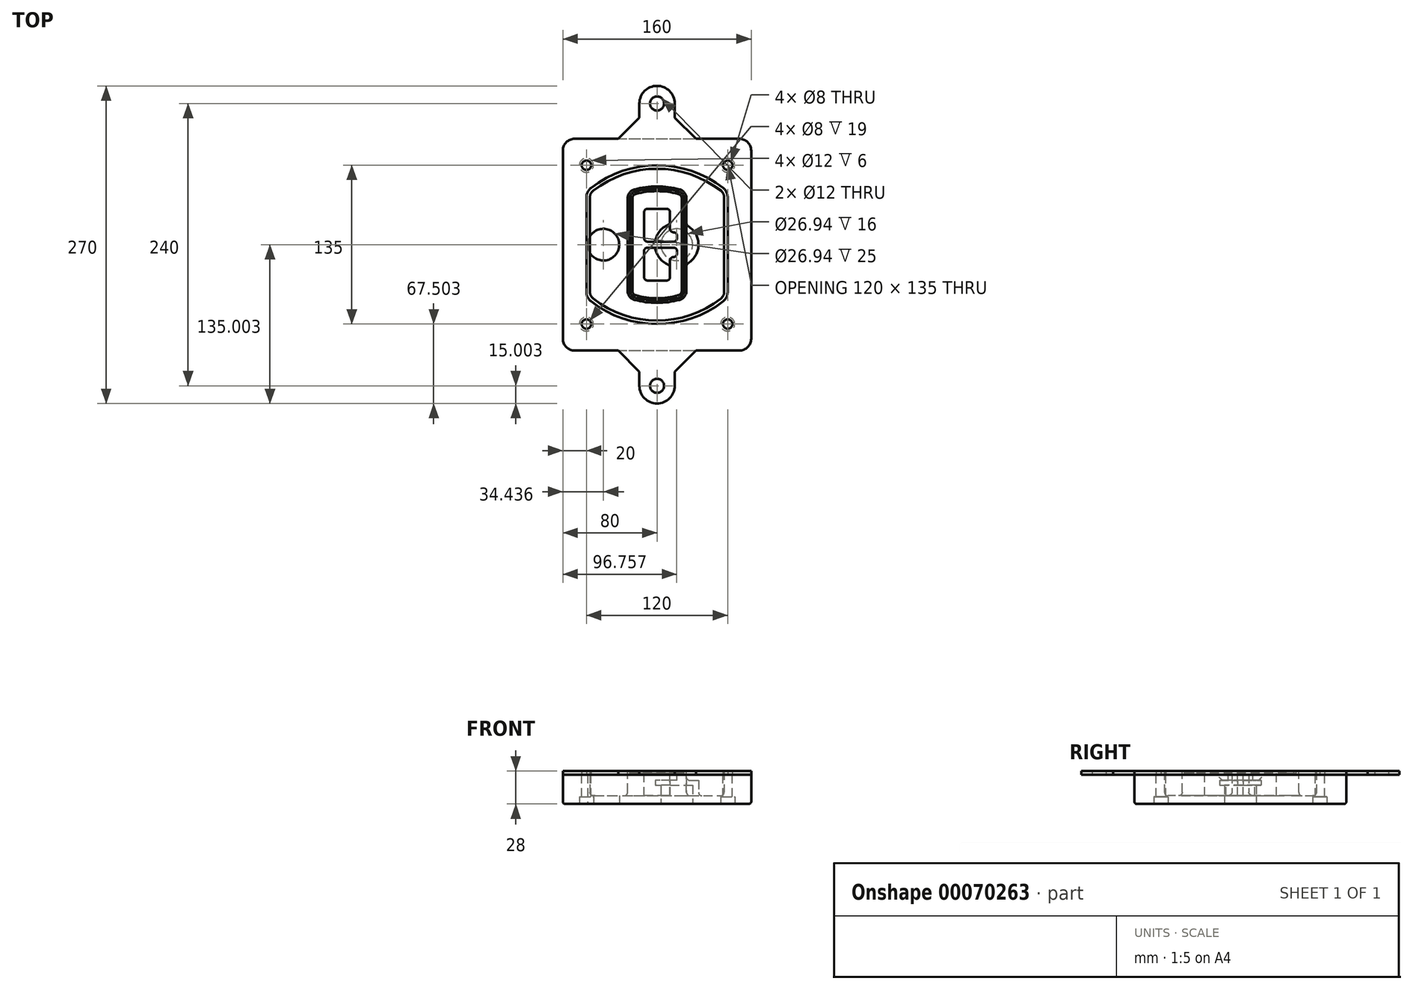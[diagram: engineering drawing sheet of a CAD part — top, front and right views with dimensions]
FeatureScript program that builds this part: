
annotation { "Feature Type Name" : "Feature", "Feature Type Description" : "" }
export const myFeature = defineFeature(function(context is Context, id is Id, definition is map)
    precondition{}
    {
        {
            var Q0;
            Q0=qCreatedBy(makeId("Top.planeOp"),FACE);
            var sketch = newSketch(context, id + "F0", { "sketchPlane" : qUnion([Q0])});
            skPoint(sketch, "E0.rect.middle", {"position": v(0, 0) * mm});
            skLineSegment(sketch, "E1.bottom", {"start": v(24.05, 28.38) * mm, "end": v(164.05, 28.38) * mm});
            skLineSegment(sketch, "E1.top", {"start": v(24.05, 208.38) * mm, "end": v(164.05, 208.38) * mm});
            skLineSegment(sketch, "E1.left", {"start": v(14.05, 38.38) * mm, "end": v(14.05, 198.38) * mm});
            skLineSegment(sketch, "E1.right", {"start": v(174.05, 38.38) * mm, "end": v(174.05, 198.38) * mm});
            skLineSegment(sketch, "E2", {"start": v(14.05, 208.38) * mm, "end": v(174.05, 28.38) * mm, "construction": true});
            skLineSegment(sketch, "E3", {"start": v(174.05, 208.38) * mm, "end": v(14.05, 28.38) * mm, "construction": true});
            skCircle(sketch, "E4", {"center": v(34.05, 185.88) * mm, "radius": 4 * mm});
            skCircle(sketch, "E5", {"center": v(154.05, 185.88) * mm, "radius": 4 * mm});
            skCircle(sketch, "E6", {"center": v(154.05, 50.88) * mm, "radius": 4 * mm});
            skCircle(sketch, "E7", {"center": v(34.05, 50.88) * mm, "radius": 4 * mm});
            skLineSegment(sketch, "E8", {"start": v(34.05, 185.88) * mm, "end": v(154.05, 185.88) * mm, "construction": true});
            skLineSegment(sketch, "E9", {"start": v(154.05, 185.88) * mm, "end": v(154.05, 50.88) * mm, "construction": true});
            skLineSegment(sketch, "E10", {"start": v(154.05, 50.88) * mm, "end": v(34.05, 50.88) * mm, "construction": true});
            skLineSegment(sketch, "E11", {"start": v(34.05, 50.88) * mm, "end": v(34.05, 185.88) * mm, "construction": true});
            skLineSegment(sketch, "E12", {"start": v(34.05, 158.68) * mm, "end": v(34.05, 78.09) * mm});
            skLineSegment(sketch, "E13", {"start": v(154.05, 158.68) * mm, "end": v(154.05, 78.09) * mm});
            skArc(sketch, "E14", {"start": v(150.2, 166.56) * mm, "mid": v(94.05, 185.88) * mm, "end": v(37.9, 166.56) * mm});
            skArc(sketch, "E15", {"start": v(37.9, 70.2) * mm, "mid": v(94.05, 50.88) * mm, "end": v(150.2, 70.2) * mm});
            skLineSegment(sketch, "E16", {"start": v(34.05, 118.38) * mm, "end": v(154.05, 118.38) * mm, "construction": true});
            skPoint(sketch, "E17.visualSharp", {"position": v(34.05, 73.38) * mm});
            skArc(sketch, "E17.filletArc", {"start": v(34.05, 78.09) * mm, "mid": v(35.06, 73.7) * mm, "end": v(37.9, 70.2) * mm});
            skPoint(sketch, "E18.visualSharp", {"position": v(34.05, 163.38) * mm});
            skArc(sketch, "E18.filletArc", {"start": v(37.9, 166.56) * mm, "mid": v(35.06, 163.06) * mm, "end": v(34.05, 158.68) * mm});
            skPoint(sketch, "E19.visualSharp", {"position": v(154.05, 163.38) * mm});
            skArc(sketch, "E19.filletArc", {"start": v(154.05, 158.68) * mm, "mid": v(153.04, 163.06) * mm, "end": v(150.2, 166.56) * mm});
            skPoint(sketch, "E20.visualSharp", {"position": v(154.05, 73.38) * mm});
            skArc(sketch, "E20.filletArc", {"start": v(150.2, 70.2) * mm, "mid": v(153.04, 73.7) * mm, "end": v(154.05, 78.09) * mm});
            skPoint(sketch, "E21.visualSharp", {"position": v(14.05, 208.38) * mm});
            skArc(sketch, "E21.filletArc", {"start": v(24.05, 208.38) * mm, "mid": v(16.98, 205.45) * mm, "end": v(14.05, 198.38) * mm});
            skPoint(sketch, "E22.visualSharp", {"position": v(174.05, 208.38) * mm});
            skArc(sketch, "E22.filletArc", {"start": v(174.05, 198.38) * mm, "mid": v(171.12, 205.45) * mm, "end": v(164.05, 208.38) * mm});
            skPoint(sketch, "E23.visualSharp", {"position": v(174.05, 28.38) * mm});
            skArc(sketch, "E23.filletArc", {"start": v(164.05, 28.38) * mm, "mid": v(171.12, 31.31) * mm, "end": v(174.05, 38.38) * mm});
            skPoint(sketch, "E24.visualSharp", {"position": v(14.05, 28.38) * mm});
            skArc(sketch, "E24.filletArc", {"start": v(14.05, 38.38) * mm, "mid": v(16.98, 31.31) * mm, "end": v(24.05, 28.38) * mm});
            skArc(sketch, "E25.0", {"start": v(151.05, 158.68) * mm, "mid": v(150.34, 161.75) * mm, "end": v(148.36, 164.2) * mm});
            skLineSegment(sketch, "E25.1", {"start": v(151.05, 158.68) * mm, "end": v(151.05, 78.09) * mm});
            skArc(sketch, "E25.2", {"start": v(148.36, 72.57) * mm, "mid": v(150.34, 75.02) * mm, "end": v(151.05, 78.09) * mm});
            skArc(sketch, "E25.3", {"start": v(39.74, 72.57) * mm, "mid": v(94.05, 53.88) * mm, "end": v(148.36, 72.57) * mm});
            skArc(sketch, "E25.4", {"start": v(37.05, 78.09) * mm, "mid": v(37.76, 75.02) * mm, "end": v(39.74, 72.57) * mm});
            skArc(sketch, "E25.5", {"start": v(148.36, 164.2) * mm, "mid": v(94.05, 182.88) * mm, "end": v(39.74, 164.2) * mm});
            skLineSegment(sketch, "E25.6", {"start": v(37.05, 158.68) * mm, "end": v(37.05, 78.09) * mm});
            skArc(sketch, "E25.7", {"start": v(39.74, 164.2) * mm, "mid": v(37.76, 161.75) * mm, "end": v(37.05, 158.68) * mm});
            skArc(sketch, "E26.0", {"start": v(35.43, 169.71) * mm, "mid": v(31.47, 164.82) * mm, "end": v(30.05, 158.68) * mm});
            skArc(sketch, "E26.1", {"start": v(152.67, 169.71) * mm, "mid": v(94.05, 189.88) * mm, "end": v(35.43, 169.71) * mm});
            skArc(sketch, "E26.2", {"start": v(158.05, 158.68) * mm, "mid": v(156.63, 164.82) * mm, "end": v(152.67, 169.71) * mm});
            skLineSegment(sketch, "E26.3", {"start": v(158.05, 158.68) * mm, "end": v(158.05, 78.09) * mm});
            skArc(sketch, "E26.4", {"start": v(152.67, 67.05) * mm, "mid": v(156.63, 71.95) * mm, "end": v(158.05, 78.09) * mm});
            skLineSegment(sketch, "E26.5", {"start": v(30.05, 158.68) * mm, "end": v(30.05, 78.09) * mm});
            skArc(sketch, "E26.6", {"start": v(35.43, 67.05) * mm, "mid": v(94.05, 46.88) * mm, "end": v(152.67, 67.05) * mm});
            skArc(sketch, "E26.7", {"start": v(30.05, 78.09) * mm, "mid": v(31.47, 71.95) * mm, "end": v(35.43, 67.05) * mm});
            skSolve(sketch);
        }
        {
            var Q0;
            Q0=makeQuery(id+"F0.imprint","IMPRINT",FACE,{"disambiguationData":[TD([[makeQuery(id+"F0.imprint","IMPRINT",EDGE,{"derivedFrom":sQuery(id+"F0.wireOp",EDGE,"E1.bottom")}),1.0]])]});
            var Q1;
            Q1=makeQuery(id+"F0.imprint","IMPRINT",FACE,{"disambiguationData":[TD([[makeQuery(id+"F0.imprint","IMPRINT",EDGE,{"derivedFrom":sQuery(id+"F0.wireOp",EDGE,"E12")}),1.0]])]});
            var Q2;
            Q2=makeQuery(id+"F0.imprint","IMPRINT",FACE,{"disambiguationData":[TD([[makeQuery(id+"F0.imprint","IMPRINT",EDGE,{"derivedFrom":sQuery(id+"F0.wireOp",EDGE,"E25.0")}),1.0]])]});
            var Q3;
            Q3=makeQuery(id+"F0.imprint","IMPRINT",FACE,{"disambiguationData":[TD([[makeQuery(id+"F0.imprint","IMPRINT",EDGE,{"derivedFrom":sQuery(id+"F0.wireOp",EDGE,"E12")}),-1.0]])]});
            extrude(context, id + "F1", {"entities" : qUnion([Q0, Q1, Q2, Q3]), "oppositeDirection" : true, "depth" : 25 * mm});
        }
        {
            var Q0;
            Q0=makeQuery(id+"F0.imprint","IMPRINT",FACE,{"disambiguationData":[TD([[makeQuery(id+"F0.imprint","IMPRINT",EDGE,{"derivedFrom":sQuery(id+"F0.wireOp",EDGE,"E12")}),1.0]])]});
            extrude(context, id + "F2", {"entities" : qUnion([Q0]), "operationType" : NewBodyOperationType.ADD, "depth" : 3 * mm});
        }
        {
            var Q0;
            Q0=makeQuery(id+"F0.imprint","IMPRINT",FACE,{"disambiguationData":[TD([[makeQuery(id+"F0.imprint","IMPRINT",EDGE,{"derivedFrom":sQuery(id+"F0.wireOp",EDGE,"E25.0")}),1.0]])]});
            extrude(context, id + "F3", {"entities" : qUnion([Q0]), "operationType" : NewBodyOperationType.REMOVE, "oppositeDirection" : true, "depth" : 18 * mm});
        }
        {
            var Q0;
            Q0=makeQuery(id+"F2.opExtrude","CAP_FACE",FACE,{"disambiguationData":[OSD([sQuery(id+"F0.wireOp",EDGE,"E12"),sQuery(id+"F0.wireOp",EDGE,"E13"),sQuery(id+"F0.wireOp",EDGE,"E14"),sQuery(id+"F0.wireOp",EDGE,"E15"),sQuery(id+"F0.wireOp",EDGE,"E17.filletArc"),sQuery(id+"F0.wireOp",EDGE,"E18.filletArc"),sQuery(id+"F0.wireOp",EDGE,"E19.filletArc"),sQuery(id+"F0.wireOp",EDGE,"E20.filletArc"),sQuery(id+"F0.wireOp",EDGE,"E25.0"),sQuery(id+"F0.wireOp",EDGE,"E25.1"),sQuery(id+"F0.wireOp",EDGE,"E25.2"),sQuery(id+"F0.wireOp",EDGE,"E25.3"),sQuery(id+"F0.wireOp",EDGE,"E25.4"),sQuery(id+"F0.wireOp",EDGE,"E25.5"),sQuery(id+"F0.wireOp",EDGE,"E25.6"),sQuery(id+"F0.wireOp",EDGE,"E25.7")])],"isStart":false});
            var sketch = newSketch(context, id + "F4", { "sketchPlane" : qUnion([Q0])});
            skArc(sketch, "E27.0", {"start": v(74.97, 71.41) * mm, "mid": v(94.05, 68.88) * mm, "end": v(113.13, 71.41) * mm});
            skArc(sketch, "E28.0", {"start": v(113.13, 165.35) * mm, "mid": v(94.05, 167.88) * mm, "end": v(74.97, 165.35) * mm});
            skLineSegment(sketch, "E29", {"start": v(69.05, 157.63) * mm, "end": v(69.05, 79.14) * mm});
            skLineSegment(sketch, "E30", {"start": v(119.05, 157.63) * mm, "end": v(119.05, 79.14) * mm});
            skLineSegment(sketch, "E31", {"start": v(69.05, 163.48) * mm, "end": v(119.05, 163.48) * mm, "construction": true});
            skLineSegment(sketch, "E32", {"start": v(69.05, 73.28) * mm, "end": v(119.05, 73.28) * mm, "construction": true});
            skPoint(sketch, "E33.visualSharp", {"position": v(69.05, 163.48) * mm});
            skArc(sketch, "E33.filletArc", {"start": v(74.97, 165.35) * mm, "mid": v(70.7, 162.5) * mm, "end": v(69.05, 157.63) * mm});
            skPoint(sketch, "E34.visualSharp", {"position": v(119.05, 163.48) * mm});
            skArc(sketch, "E34.filletArc", {"start": v(119.05, 157.63) * mm, "mid": v(117.4, 162.5) * mm, "end": v(113.13, 165.35) * mm});
            skPoint(sketch, "E35.visualSharp", {"position": v(119.05, 73.28) * mm});
            skArc(sketch, "E35.filletArc", {"start": v(113.13, 71.41) * mm, "mid": v(117.4, 74.27) * mm, "end": v(119.05, 79.14) * mm});
            skPoint(sketch, "E36.visualSharp", {"position": v(69.05, 73.28) * mm});
            skArc(sketch, "E36.filletArc", {"start": v(69.05, 79.14) * mm, "mid": v(70.7, 74.27) * mm, "end": v(74.97, 71.41) * mm});
            skArc(sketch, "E37.0", {"start": v(148.36, 164.2) * mm, "mid": v(94.05, 182.88) * mm, "end": v(39.74, 164.2) * mm});
            skArc(sketch, "E37.1", {"start": v(39.74, 164.2) * mm, "mid": v(37.76, 161.75) * mm, "end": v(37.05, 158.68) * mm});
            skLineSegment(sketch, "E37.2", {"start": v(37.05, 158.68) * mm, "end": v(37.05, 78.09) * mm});
            skArc(sketch, "E37.3", {"start": v(37.05, 78.09) * mm, "mid": v(37.76, 75.02) * mm, "end": v(39.74, 72.57) * mm});
            skArc(sketch, "E37.4", {"start": v(39.74, 72.57) * mm, "mid": v(94.05, 53.88) * mm, "end": v(148.36, 72.57) * mm});
            skArc(sketch, "E37.5", {"start": v(148.36, 72.57) * mm, "mid": v(150.34, 75.02) * mm, "end": v(151.05, 78.09) * mm});
            skLineSegment(sketch, "E37.6", {"start": v(151.05, 158.68) * mm, "end": v(151.05, 78.09) * mm});
            skArc(sketch, "E37.7", {"start": v(151.05, 158.68) * mm, "mid": v(150.34, 161.75) * mm, "end": v(148.36, 164.2) * mm});
            skLineSegment(sketch, "E38.0", {"start": v(117.05, 157.63) * mm, "end": v(117.05, 79.14) * mm});
            skArc(sketch, "E38.1", {"start": v(112.61, 73.34) * mm, "mid": v(115.81, 75.49) * mm, "end": v(117.05, 79.14) * mm});
            skArc(sketch, "E38.2", {"start": v(75.49, 73.34) * mm, "mid": v(94.05, 70.88) * mm, "end": v(112.61, 73.34) * mm});
            skArc(sketch, "E38.3", {"start": v(71.05, 79.14) * mm, "mid": v(72.29, 75.49) * mm, "end": v(75.49, 73.34) * mm});
            skLineSegment(sketch, "E38.4", {"start": v(71.05, 157.63) * mm, "end": v(71.05, 79.14) * mm});
            skArc(sketch, "E38.5", {"start": v(117.05, 157.63) * mm, "mid": v(115.81, 161.28) * mm, "end": v(112.61, 163.42) * mm});
            skArc(sketch, "E38.6", {"start": v(75.49, 163.42) * mm, "mid": v(72.29, 161.28) * mm, "end": v(71.05, 157.63) * mm});
            skArc(sketch, "E38.7", {"start": v(112.61, 163.42) * mm, "mid": v(94.05, 165.88) * mm, "end": v(75.49, 163.42) * mm});
            skArc(sketch, "E39.0", {"start": v(115.05, 157.63) * mm, "mid": v(114.23, 160.06) * mm, "end": v(112.1, 161.5) * mm});
            skLineSegment(sketch, "E39.1", {"start": v(115.05, 157.63) * mm, "end": v(115.05, 79.14) * mm});
            skArc(sketch, "E39.2", {"start": v(112.1, 75.27) * mm, "mid": v(114.23, 76.7) * mm, "end": v(115.05, 79.14) * mm});
            skArc(sketch, "E39.3", {"start": v(76, 75.27) * mm, "mid": v(94.05, 72.88) * mm, "end": v(112.1, 75.27) * mm});
            skArc(sketch, "E39.4", {"start": v(73.05, 79.14) * mm, "mid": v(73.87, 76.7) * mm, "end": v(76, 75.27) * mm});
            skArc(sketch, "E39.5", {"start": v(112.1, 161.5) * mm, "mid": v(94.05, 163.88) * mm, "end": v(76, 161.5) * mm});
            skLineSegment(sketch, "E39.6", {"start": v(73.05, 157.63) * mm, "end": v(73.05, 79.14) * mm});
            skArc(sketch, "E39.7", {"start": v(76, 161.5) * mm, "mid": v(73.87, 160.06) * mm, "end": v(73.05, 157.63) * mm});
            skLineSegment(sketch, "E40", {"start": v(69.05, 118.38) * mm, "end": v(119.05, 118.38) * mm, "construction": true});
            skLineSegment(sketch, "E41", {"start": v(83.05, 123.88) * mm, "end": v(83.05, 145.88) * mm});
            skLineSegment(sketch, "E42", {"start": v(86.05, 148.88) * mm, "end": v(102.05, 148.88) * mm});
            skLineSegment(sketch, "E43", {"start": v(105.05, 145.88) * mm, "end": v(105.05, 131.88) * mm});
            skLineSegment(sketch, "E44", {"start": v(108.05, 128.88) * mm, "end": v(108.05, 128.88) * mm});
            skLineSegment(sketch, "E45", {"start": v(111.05, 125.88) * mm, "end": v(111.05, 123.88) * mm});
            skLineSegment(sketch, "E46", {"start": v(108.05, 120.88) * mm, "end": v(86.05, 120.88) * mm});
            skPoint(sketch, "E47.visualSharp", {"position": v(83.05, 148.88) * mm});
            skArc(sketch, "E47.filletArc", {"start": v(86.05, 148.88) * mm, "mid": v(83.93, 148) * mm, "end": v(83.05, 145.88) * mm});
            skPoint(sketch, "E48.visualSharp", {"position": v(105.05, 148.88) * mm});
            skArc(sketch, "E48.filletArc", {"start": v(105.05, 145.88) * mm, "mid": v(104.17, 148) * mm, "end": v(102.05, 148.88) * mm});
            skPoint(sketch, "E49.visualSharp", {"position": v(105.05, 128.88) * mm});
            skArc(sketch, "E49.filletArc", {"start": v(105.05, 131.88) * mm, "mid": v(105.93, 129.76) * mm, "end": v(108.05, 128.88) * mm});
            skPoint(sketch, "E50.visualSharp", {"position": v(111.05, 128.88) * mm});
            skArc(sketch, "E50.filletArc", {"start": v(111.05, 125.88) * mm, "mid": v(110.17, 128) * mm, "end": v(108.05, 128.88) * mm});
            skPoint(sketch, "E51.visualSharp", {"position": v(111.05, 120.88) * mm});
            skArc(sketch, "E51.filletArc", {"start": v(108.05, 120.88) * mm, "mid": v(110.17, 121.76) * mm, "end": v(111.05, 123.88) * mm});
            skPoint(sketch, "E52.visualSharp", {"position": v(83.05, 120.88) * mm});
            skArc(sketch, "E52.filletArc", {"start": v(83.05, 123.88) * mm, "mid": v(83.93, 121.76) * mm, "end": v(86.05, 120.88) * mm});
            skLineSegment(sketch, "E53.0.MirrorCS", {"start": v(108.05, 115.88) * mm, "end": v(86.05, 115.88) * mm});
            skArc(sketch, "E54.0.MirrorCS", {"start": v(83.05, 112.88) * mm, "mid": v(83.93, 115) * mm, "end": v(86.05, 115.88) * mm});
            skLineSegment(sketch, "E55.0.MirrorCS", {"start": v(83.05, 112.88) * mm, "end": v(83.05, 90.88) * mm});
            skArc(sketch, "E56.0.MirrorCS", {"start": v(86.05, 87.88) * mm, "mid": v(83.93, 88.76) * mm, "end": v(83.05, 90.88) * mm});
            skLineSegment(sketch, "E57.0.MirrorCS", {"start": v(86.05, 87.88) * mm, "end": v(102.05, 87.88) * mm});
            skArc(sketch, "E58.0.MirrorCS", {"start": v(105.05, 90.88) * mm, "mid": v(104.17, 88.76) * mm, "end": v(102.05, 87.88) * mm});
            skLineSegment(sketch, "E59.0.MirrorCS", {"start": v(105.05, 90.88) * mm, "end": v(105.05, 104.88) * mm});
            skArc(sketch, "E60.0.MirrorCS", {"start": v(105.05, 104.88) * mm, "mid": v(105.93, 107) * mm, "end": v(108.05, 107.88) * mm});
            skArc(sketch, "E61.0.MirrorCS", {"start": v(111.05, 110.88) * mm, "mid": v(110.17, 108.76) * mm, "end": v(108.05, 107.88) * mm});
            skLineSegment(sketch, "E62.0.MirrorCS", {"start": v(111.05, 110.88) * mm, "end": v(111.05, 112.88) * mm});
            skArc(sketch, "E63.0.MirrorCS", {"start": v(108.05, 115.88) * mm, "mid": v(110.17, 115) * mm, "end": v(111.05, 112.88) * mm});
            skSolve(sketch);
        }
        {
            var Q0;
            Q0=makeQuery(id+"F4.imprint","IMPRINT",FACE,{"disambiguationData":[TD([[makeQuery(id+"F4.imprint","IMPRINT",EDGE,{"derivedFrom":sQuery(id+"F4.wireOp",EDGE,"E27.0")}),1.0]])]});
            var Q1;
            Q1=makeQuery(id+"F4.imprint","IMPRINT",FACE,{"disambiguationData":[TD([[makeQuery(id+"F4.imprint","IMPRINT",EDGE,{"derivedFrom":sQuery(id+"F4.wireOp",EDGE,"E38.0")}),-1.0]])]});
            var Q2;
            Q2=makeQuery(id+"F4.imprint","IMPRINT",FACE,{"disambiguationData":[TD([[makeQuery(id+"F4.imprint","IMPRINT",EDGE,{"derivedFrom":sQuery(id+"F4.wireOp",EDGE,"E39.0")}),1.0]])]});
            extrude(context, id + "F5", {"entities" : qUnion([Q0, Q1, Q2]), "operationType" : NewBodyOperationType.ADD, "endBound" : BoundingType.UP_TO_NEXT, "oppositeDirection" : true, "depth" : 25 * mm});
        }
        {
            var Q0;
            Q0=makeQuery(id+"F4.imprint","IMPRINT",FACE,{"disambiguationData":[TD([[makeQuery(id+"F4.imprint","IMPRINT",EDGE,{"derivedFrom":sQuery(id+"F4.wireOp",EDGE,"E38.0")}),-1.0]])]});
            extrude(context, id + "F6", {"entities" : qUnion([Q0]), "operationType" : NewBodyOperationType.REMOVE, "oppositeDirection" : true, "depth" : 2 * mm});
        }
        {
            var Q0;
            Q0=makeQuery(id+"F1.opExtrude","CAP_FACE",FACE,{"disambiguationData":[OSD([sQuery(id+"F0.wireOp",EDGE,"E1.bottom"),sQuery(id+"F0.wireOp",EDGE,"E1.top"),sQuery(id+"F0.wireOp",EDGE,"E1.left"),sQuery(id+"F0.wireOp",EDGE,"E1.right"),sQuery(id+"F0.wireOp",EDGE,"E4"),sQuery(id+"F0.wireOp",EDGE,"E5"),sQuery(id+"F0.wireOp",EDGE,"E6"),sQuery(id+"F0.wireOp",EDGE,"E7"),sQuery(id+"F0.wireOp",EDGE,"E21.filletArc"),sQuery(id+"F0.wireOp",EDGE,"E22.filletArc"),sQuery(id+"F0.wireOp",EDGE,"E23.filletArc"),sQuery(id+"F0.wireOp",EDGE,"E24.filletArc")])],"isStart":false});
            var sketch = newSketch(context, id + "F7", { "sketchPlane" : qUnion([Q0])});
            skCircle(sketch, "E64", {"center": v(110.8, -118.38) * mm, "radius": 13.47 * mm});
            skCircle(sketch, "E65", {"center": v(48.49, -118.38) * mm, "radius": 13.47 * mm});
            skLineSegment(sketch, "E66", {"start": v(174.05, -118.38) * mm, "end": v(14.05, -118.38) * mm});
            skCircle(sketch, "E67", {"center": v(110.8, -118.38) * mm, "radius": 18.47 * mm});
            skCircle(sketch, "E68", {"center": v(154.05, -185.88) * mm, "radius": 6 * mm});
            skCircle(sketch, "E69", {"center": v(34.05, -185.88) * mm, "radius": 6 * mm});
            skCircle(sketch, "E70", {"center": v(34.05, -50.88) * mm, "radius": 6 * mm});
            skCircle(sketch, "E71", {"center": v(154.05, -50.88) * mm, "radius": 6 * mm});
            skSolve(sketch);
        }
        {
            var Q0;
            {var subQ1=sQuery(id+"F7.wireOp",EDGE,"E66");var subQ4=sQuery(id+"F7.wireOp",EDGE,"E64");var subQ6=makeQuery(id+"F7.imprint","INTERSECT",VERTEX,{"disambiguationData":[OD(0.0)],"derivedFrom":[subQ4,subQ1]});Q0=makeQuery(id+"F7.imprint","IMPRINT",FACE,{"disambiguationData":[TD([[makeQuery(id+"F7.imprint","IMPRINT",EDGE,{"disambiguationData":[TD([[subQ6,-1.0]])],"derivedFrom":subQ4}),-1.0]])]});}
            var Q1;
            {var subQ0=sQuery(id+"F7.wireOp",EDGE,"E66");var subQ1=sQuery(id+"F7.wireOp",EDGE,"E64");var subQ3=makeQuery(id+"F7.imprint","INTERSECT",VERTEX,{"disambiguationData":[OD(0.0)],"derivedFrom":[subQ1,subQ0]});Q1=makeQuery(id+"F7.imprint","IMPRINT",FACE,{"disambiguationData":[TD([[makeQuery(id+"F7.imprint","IMPRINT",EDGE,{"disambiguationData":[TD([[subQ3,-1.0]])],"derivedFrom":subQ1}),1.0]])]});}
            var Q2;
            {var subQ0=sQuery(id+"F7.wireOp",EDGE,"E66");var subQ1=sQuery(id+"F7.wireOp",EDGE,"E64");var subQ3=makeQuery(id+"F7.imprint","INTERSECT",VERTEX,{"disambiguationData":[OD(0.0)],"derivedFrom":[subQ1,subQ0]});Q2=makeQuery(id+"F7.imprint","IMPRINT",FACE,{"disambiguationData":[TD([[makeQuery(id+"F7.imprint","IMPRINT",EDGE,{"disambiguationData":[TD([[subQ3,1.0]])],"derivedFrom":subQ1}),1.0]])]});}
            var Q3;
            {var subQ1=sQuery(id+"F7.wireOp",EDGE,"E66");var subQ4=sQuery(id+"F7.wireOp",EDGE,"E64");var subQ6=makeQuery(id+"F7.imprint","INTERSECT",VERTEX,{"disambiguationData":[OD(0.0)],"derivedFrom":[subQ4,subQ1]});Q3=makeQuery(id+"F7.imprint","IMPRINT",FACE,{"disambiguationData":[TD([[makeQuery(id+"F7.imprint","IMPRINT",EDGE,{"disambiguationData":[TD([[subQ6,1.0]])],"derivedFrom":subQ4}),-1.0]])]});}
            extrude(context, id + "F8", {"entities" : qUnion([Q0, Q1, Q2, Q3]), "operationType" : NewBodyOperationType.ADD, "oppositeDirection" : true, "depth" : 20 * mm});
        }
        {
            var Q0;
            {var subQ0=sQuery(id+"F7.wireOp",EDGE,"E66");var subQ1=sQuery(id+"F7.wireOp",EDGE,"E64");var subQ3=makeQuery(id+"F7.imprint","INTERSECT",VERTEX,{"disambiguationData":[OD(0.0)],"derivedFrom":[subQ1,subQ0]});Q0=makeQuery(id+"F7.imprint","IMPRINT",FACE,{"disambiguationData":[TD([[makeQuery(id+"F7.imprint","IMPRINT",EDGE,{"disambiguationData":[TD([[subQ3,-1.0]])],"derivedFrom":subQ1}),1.0]])]});}
            var Q1;
            {var subQ0=sQuery(id+"F7.wireOp",EDGE,"E66");var subQ1=sQuery(id+"F7.wireOp",EDGE,"E64");var subQ3=makeQuery(id+"F7.imprint","INTERSECT",VERTEX,{"disambiguationData":[OD(0.0)],"derivedFrom":[subQ1,subQ0]});Q1=makeQuery(id+"F7.imprint","IMPRINT",FACE,{"disambiguationData":[TD([[makeQuery(id+"F7.imprint","IMPRINT",EDGE,{"disambiguationData":[TD([[subQ3,1.0]])],"derivedFrom":subQ1}),1.0]])]});}
            extrude(context, id + "F9", {"entities" : qUnion([Q0, Q1]), "operationType" : NewBodyOperationType.REMOVE, "oppositeDirection" : true, "depth" : 16 * mm});
        }
        {
            var Q0;
            {var subQ0=sQuery(id+"F7.wireOp",EDGE,"E66");var subQ1=sQuery(id+"F7.wireOp",EDGE,"E65");var subQ3=makeQuery(id+"F7.imprint","INTERSECT",VERTEX,{"disambiguationData":[OD(0.0)],"derivedFrom":[subQ1,subQ0]});Q0=makeQuery(id+"F7.imprint","IMPRINT",FACE,{"disambiguationData":[TD([[makeQuery(id+"F7.imprint","IMPRINT",EDGE,{"disambiguationData":[TD([[subQ3,-1.0]])],"derivedFrom":subQ1}),1.0]])]});}
            var Q1;
            {var subQ0=sQuery(id+"F7.wireOp",EDGE,"E66");var subQ1=sQuery(id+"F7.wireOp",EDGE,"E65");var subQ3=makeQuery(id+"F7.imprint","INTERSECT",VERTEX,{"disambiguationData":[OD(0.0)],"derivedFrom":[subQ1,subQ0]});Q1=makeQuery(id+"F7.imprint","IMPRINT",FACE,{"disambiguationData":[TD([[makeQuery(id+"F7.imprint","IMPRINT",EDGE,{"disambiguationData":[TD([[subQ3,1.0]])],"derivedFrom":subQ1}),1.0]])]});}
            extrude(context, id + "F10", {"entities" : qUnion([Q0, Q1]), "operationType" : NewBodyOperationType.REMOVE, "oppositeDirection" : true, "depth" : 25 * mm});
        }
        {
            var Q0;
            Q0=makeQuery(id+"F7.imprint","IMPRINT",FACE,{"disambiguationData":[TD([[makeQuery(id+"F7.imprint","IMPRINT",EDGE,{"derivedFrom":sQuery(id+"F7.wireOp",EDGE,"E68")}),1.0]])]});
            var Q1;
            Q1=makeQuery(id+"F7.imprint","IMPRINT",FACE,{"disambiguationData":[TD([[makeQuery(id+"F7.imprint","IMPRINT",EDGE,{"derivedFrom":makeQuery(id+"F1.opExtrude","CAP_EDGE",EDGE,{"disambiguationData":[OSD([sQuery(id+"F0.wireOp",EDGE,"E5")])],"isStart":false})}),-1.0]])]});
            var Q2;
            Q2=makeQuery(id+"F7.imprint","IMPRINT",FACE,{"disambiguationData":[TD([[makeQuery(id+"F7.imprint","IMPRINT",EDGE,{"derivedFrom":sQuery(id+"F7.wireOp",EDGE,"E69")}),1.0]])]});
            var Q3;
            Q3=makeQuery(id+"F7.imprint","IMPRINT",FACE,{"disambiguationData":[TD([[makeQuery(id+"F7.imprint","IMPRINT",EDGE,{"derivedFrom":makeQuery(id+"F1.opExtrude","CAP_EDGE",EDGE,{"disambiguationData":[OSD([sQuery(id+"F0.wireOp",EDGE,"E4")])],"isStart":false})}),-1.0]])]});
            var Q4;
            Q4=makeQuery(id+"F7.imprint","IMPRINT",FACE,{"disambiguationData":[TD([[makeQuery(id+"F7.imprint","IMPRINT",EDGE,{"derivedFrom":sQuery(id+"F7.wireOp",EDGE,"E70")}),1.0]])]});
            var Q5;
            Q5=makeQuery(id+"F7.imprint","IMPRINT",FACE,{"disambiguationData":[TD([[makeQuery(id+"F7.imprint","IMPRINT",EDGE,{"derivedFrom":makeQuery(id+"F1.opExtrude","CAP_EDGE",EDGE,{"disambiguationData":[OSD([sQuery(id+"F0.wireOp",EDGE,"E7")])],"isStart":false})}),-1.0]])]});
            var Q6;
            Q6=makeQuery(id+"F7.imprint","IMPRINT",FACE,{"disambiguationData":[TD([[makeQuery(id+"F7.imprint","IMPRINT",EDGE,{"derivedFrom":sQuery(id+"F7.wireOp",EDGE,"E71")}),1.0]])]});
            var Q7;
            Q7=makeQuery(id+"F7.imprint","IMPRINT",FACE,{"disambiguationData":[TD([[makeQuery(id+"F7.imprint","IMPRINT",EDGE,{"derivedFrom":makeQuery(id+"F1.opExtrude","CAP_EDGE",EDGE,{"disambiguationData":[OSD([sQuery(id+"F0.wireOp",EDGE,"E6")])],"isStart":false})}),-1.0]])]});
            extrude(context, id + "F11", {"entities" : qUnion([Q0, Q1, Q2, Q3, Q4, Q5, Q6, Q7]), "operationType" : NewBodyOperationType.REMOVE, "oppositeDirection" : true, "depth" : 6 * mm});
        }
        {
            var Q0;
            Q0=makeQuery(id+"F9.boolean.opBoolean","COPY",FACE,{"derivedFrom":makeQuery(id+"F9.opExtrude","CAP_FACE",FACE,{"disambiguationData":[OSD([sQuery(id+"F7.wireOp",EDGE,"E64")])],"isStart":false})});
            var sketch = newSketch(context, id + "F12", { "sketchPlane" : qUnion([Q0])});
            skArc(sketch, "E72.0", {"start": v(105.05, -100.83) * mm, "mid": v(96.62, -106.56) * mm, "end": v(92.5, -115.88) * mm});
            skArc(sketch, "E72.1", {"start": v(92.5, -120.88) * mm, "mid": v(96.62, -130.2) * mm, "end": v(105.05, -135.93) * mm});
            skLineSegment(sketch, "E73", {"start": v(92.5, -120.88) * mm, "end": v(108.05, -120.88) * mm});
            skLineSegment(sketch, "E74.0", {"start": v(108.05, -115.88) * mm, "end": v(92.5, -115.88) * mm});
            skArc(sketch, "E74.1", {"start": v(108.05, -115.88) * mm, "mid": v(110.17, -115) * mm, "end": v(111.05, -112.88) * mm});
            skLineSegment(sketch, "E74.2", {"start": v(111.05, -110.88) * mm, "end": v(111.05, -112.88) * mm});
            skArc(sketch, "E74.3", {"start": v(111.05, -110.88) * mm, "mid": v(110.17, -108.76) * mm, "end": v(108.05, -107.88) * mm});
            skArc(sketch, "E74.4", {"start": v(105.05, -104.88) * mm, "mid": v(105.93, -107) * mm, "end": v(108.05, -107.88) * mm});
            skLineSegment(sketch, "E74.5", {"start": v(105.05, -100.83) * mm, "end": v(105.05, -104.88) * mm});
            skLineSegment(sketch, "E74.7", {"start": v(108.05, -120.88) * mm, "end": v(92.5, -120.88) * mm});
            skArc(sketch, "E74.8", {"start": v(108.05, -120.88) * mm, "mid": v(110.17, -121.76) * mm, "end": v(111.05, -123.88) * mm});
            skLineSegment(sketch, "E74.9", {"start": v(111.05, -125.88) * mm, "end": v(111.05, -123.88) * mm});
            skArc(sketch, "E74.10", {"start": v(111.05, -125.88) * mm, "mid": v(110.17, -128) * mm, "end": v(108.05, -128.88) * mm});
            skArc(sketch, "E74.11", {"start": v(105.05, -131.88) * mm, "mid": v(105.93, -129.76) * mm, "end": v(108.05, -128.88) * mm});
            skLineSegment(sketch, "E74.12", {"start": v(105.05, -135.93) * mm, "end": v(105.05, -131.88) * mm});
            skPoint(sketch, "E75.orphan", {"position": v(105.05, -145.88) * mm});
            skPoint(sketch, "E76.orphan", {"position": v(86.05, -120.88) * mm});
            skPoint(sketch, "E77.orphan", {"position": v(86.05, -115.88) * mm});
            skPoint(sketch, "E78.orphan", {"position": v(105.05, -90.88) * mm});
            skSolve(sketch);
        }
        {
            var Q0;
            {var subQ7=sQuery(id+"F12.wireOp",EDGE,"E72.0");var subQ14=sQuery(id+"F12.wireOp",EDGE,"E72.1");var subQ16=sQuery(id+"F12.wireOp",EDGE,"E74.1");var subQ18=sQuery(id+"F12.wireOp",EDGE,"E74.8");Q0=qUnion([makeQuery(id+"F12.imprint","IMPRINT",FACE,{"disambiguationData":[TD([[makeQuery(id+"F12.imprint","IMPRINT",EDGE,{"derivedFrom":subQ7}),1.0]])]}),makeQuery(id+"F12.imprint","IMPRINT",FACE,{"disambiguationData":[TD([[makeQuery(id+"F12.imprint","IMPRINT",EDGE,{"derivedFrom":subQ14}),1.0]])]}),makeQuery(id+"F12.imprint","IMPRINT",FACE,{"disambiguationData":[TD([[makeQuery(id+"F12.imprint","IMPRINT",EDGE,{"derivedFrom":subQ16}),1.0]])]}),makeQuery(id+"F12.imprint","IMPRINT",FACE,{"disambiguationData":[TD([[makeQuery(id+"F12.imprint","IMPRINT",EDGE,{"derivedFrom":subQ18}),-1.0]])]})]);}
            var Q1;
            Q1=makeQuery(id+"F5.boolean.opBoolean","SPLIT",FACE,{"disambiguationData":[TD([makeQuery(id+"F5.opExtrude","SWEPT_FACE",FACE,{"disambiguationData":[OSD([sQuery(id+"F4.wireOp",EDGE,"E41")])]})])],"derivedFrom":makeQuery(id+"F3.boolean.opBoolean","COPY",FACE,{"derivedFrom":makeQuery(id+"F3.opExtrude","CAP_FACE",FACE,{"disambiguationData":[OSD([sQuery(id+"F0.wireOp",EDGE,"E25.0"),sQuery(id+"F0.wireOp",EDGE,"E25.1"),sQuery(id+"F0.wireOp",EDGE,"E25.2"),sQuery(id+"F0.wireOp",EDGE,"E25.3"),sQuery(id+"F0.wireOp",EDGE,"E25.4"),sQuery(id+"F0.wireOp",EDGE,"E25.5"),sQuery(id+"F0.wireOp",EDGE,"E25.6"),sQuery(id+"F0.wireOp",EDGE,"E25.7")])],"isStart":false})})});
            extrude(context, id + "F13", {"entities" : qUnion([Q0]), "operationType" : NewBodyOperationType.REMOVE, "endBound" : BoundingType.UP_TO_SURFACE, "endBoundEntityFace" : qUnion([Q1]), "depth" : 25 * mm});
        }
        {
            var Q0;
            Q0=makeQuery(id+"F3.boolean.opBoolean","COPY",EDGE,{"derivedFrom":makeQuery(id+"F3.opExtrude","CAP_EDGE",EDGE,{"disambiguationData":[OSD([sQuery(id+"F0.wireOp",EDGE,"E25.6")])],"isStart":false})});
            var Q1;
            Q1=makeQuery(id+"F8.boolean.opBoolean","INTERSECT",EDGE,{"derivedFrom":[makeQuery(id+"F5.opExtrude","SWEPT_FACE",FACE,{"disambiguationData":[OSD([sQuery(id+"F4.wireOp",EDGE,"E30")])]}),makeQuery(id+"F8.opExtrude","CAP_FACE",FACE,{"disambiguationData":[OSD([sQuery(id+"F7.wireOp",EDGE,"E67")])],"isStart":false})]});
            var Q2;
            Q2=makeQuery(id+"F8.boolean.opBoolean","INTERSECT",EDGE,{"disambiguationData":[OD(1.0)],"derivedFrom":[makeQuery(id+"F5.opExtrude","SWEPT_FACE",FACE,{"disambiguationData":[OSD([sQuery(id+"F4.wireOp",EDGE,"E30")])]}),makeQuery(id+"F8.opExtrude","SWEPT_FACE",FACE,{"disambiguationData":[OSD([sQuery(id+"F7.wireOp",EDGE,"E67")])]})]});
            var Q3;
            {var subQ0=sQuery(id+"F4.wireOp",EDGE,"E30");Q3=makeQuery(id+"F8.boolean.opBoolean","SPLIT",EDGE,{"disambiguationData":[TD([makeQuery(id+"F5.opExtrude","SWEPT_FACE",FACE,{"disambiguationData":[OSD([sQuery(id+"F4.wireOp",EDGE,"E35.filletArc")])]})])],"derivedFrom":makeQuery(id+"F5.opExtrude","CAP_EDGE",EDGE,{"disambiguationData":[OSD([subQ0])],"isStart":false})});}
            var Q4;
            {var subQ0=sQuery(id+"F0.wireOp",EDGE,"E25.7");var subQ1=sQuery(id+"F0.wireOp",EDGE,"E25.1");var subQ2=sQuery(id+"F0.wireOp",EDGE,"E25.6");var subQ3=sQuery(id+"F0.wireOp",EDGE,"E25.5");var subQ4=sQuery(id+"F0.wireOp",EDGE,"E25.4");var subQ5=sQuery(id+"F0.wireOp",EDGE,"E25.0");var subQ6=sQuery(id+"F0.wireOp",EDGE,"E25.2");var subQ7=sQuery(id+"F0.wireOp",EDGE,"E25.3");Q4=makeQuery(id+"F8.boolean.opBoolean","INTERSECT",EDGE,{"derivedFrom":[makeQuery(id+"F5.boolean.opBoolean","SPLIT",FACE,{"disambiguationData":[TD([makeQuery(id+"F2.opExtrude","SWEPT_FACE",FACE,{"disambiguationData":[OSD([subQ5])]})])],"derivedFrom":makeQuery(id+"F3.boolean.opBoolean","COPY",FACE,{"derivedFrom":makeQuery(id+"F3.opExtrude","CAP_FACE",FACE,{"disambiguationData":[OSD([subQ5,subQ1,subQ6,subQ7,subQ4,subQ3,subQ2,subQ0])],"isStart":false})})}),makeQuery(id+"F8.opExtrude","SWEPT_FACE",FACE,{"disambiguationData":[OSD([sQuery(id+"F7.wireOp",EDGE,"E67")])]})]});}
            var Q5;
            Q5=makeQuery(id+"F8.boolean.opBoolean","INTERSECT",EDGE,{"disambiguationData":[OD(0.0)],"derivedFrom":[makeQuery(id+"F5.opExtrude","SWEPT_FACE",FACE,{"disambiguationData":[OSD([sQuery(id+"F4.wireOp",EDGE,"E30")])]}),makeQuery(id+"F8.opExtrude","SWEPT_FACE",FACE,{"disambiguationData":[OSD([sQuery(id+"F7.wireOp",EDGE,"E67")])]})]});
            fillet(context, id + "F14", {"entities" : qUnion([Q0, Q1, Q2, Q3, Q4, Q5]), "radius" : 3 * mm, "tangentPropagation" : true, "allowEdgeOverflow" : false});
        }
        {
            var Q0;
            Q0=makeQuery(id+"F1.opExtrude","CAP_EDGE",EDGE,{"disambiguationData":[OSD([sQuery(id+"F0.wireOp",EDGE,"E1.bottom")])],"isStart":false});
            fillet(context, id + "F15", {"entities" : qUnion([Q0]), "radius" : 2 * mm, "tangentPropagation" : true, "allowEdgeOverflow" : false});
        }
        {
            var Q0;
            {var subQ0=sQuery(id+"F0.wireOp",EDGE,"E22.filletArc");var subQ1=sQuery(id+"F0.wireOp",EDGE,"E7");var subQ2=sQuery(id+"F0.wireOp",EDGE,"E6");var subQ3=sQuery(id+"F0.wireOp",EDGE,"E5");var subQ4=sQuery(id+"F0.wireOp",EDGE,"E4");var subQ5=sQuery(id+"F0.wireOp",EDGE,"E1.bottom");var subQ6=sQuery(id+"F0.wireOp",EDGE,"E21.filletArc");var subQ7=sQuery(id+"F0.wireOp",EDGE,"E1.top");var subQ8=sQuery(id+"F0.wireOp",EDGE,"E1.left");var subQ9=sQuery(id+"F0.wireOp",EDGE,"E1.right");var subQ10=sQuery(id+"F0.wireOp",EDGE,"E23.filletArc");var subQ11=sQuery(id+"F0.wireOp",EDGE,"E24.filletArc");Q0=makeQuery(id+"F2.boolean.opBoolean","SPLIT",FACE,{"disambiguationData":[TD([makeQuery(id+"F1.opExtrude","SWEPT_FACE",FACE,{"disambiguationData":[OSD([subQ5])]})])],"derivedFrom":makeQuery(id+"F1.opExtrude","CAP_FACE",FACE,{"disambiguationData":[OSD([subQ5,subQ7,subQ8,subQ9,subQ4,subQ3,subQ2,subQ1,subQ6,subQ0,subQ10,subQ11])],"isStart":true})});}
            var sketch = newSketch(context, id + "F16", { "sketchPlane" : qUnion([Q0])});
            skLineSegment(sketch, "E79", {"start": v(94.05, 28.38) * mm, "end": v(94.05, -1.62) * mm, "construction": true});
            skCircle(sketch, "E80", {"center": v(94.05, -1.62) * mm, "radius": 6 * mm});
            skArc(sketch, "E81", {"start": v(79.05, -1.62) * mm, "mid": v(94.05, -16.62) * mm, "end": v(109.05, -1.62) * mm});
            skLineSegment(sketch, "E82", {"start": v(68.14, 10.38) * mm, "end": v(109.25, 10.38) * mm, "construction": true});
            skLineSegment(sketch, "E83", {"start": v(79.05, -1.62) * mm, "end": v(79.05, 10.38) * mm});
            skLineSegment(sketch, "E84.MirrorCS", {"start": v(109.05, -1.62) * mm, "end": v(109.05, 10.38) * mm});
            skLineSegment(sketch, "E85", {"start": v(79.05, 10.38) * mm, "end": v(61.05, 28.38) * mm});
            skLineSegment(sketch, "E86.MirrorCS", {"start": v(109.05, 10.38) * mm, "end": v(127.05, 28.38) * mm});
            skLineSegment(sketch, "E87", {"start": v(14.05, 118.38) * mm, "end": v(174.05, 118.38) * mm, "construction": true});
            skLineSegment(sketch, "E88.MirrorCS", {"start": v(109.05, 238.38) * mm, "end": v(109.05, 226.38) * mm});
            skCircle(sketch, "E89.MirrorC", {"center": v(94.05, 238.38) * mm, "radius": 6 * mm});
            skLineSegment(sketch, "E90.MirrorCS", {"start": v(109.05, 226.38) * mm, "end": v(127.05, 208.38) * mm});
            skLineSegment(sketch, "E91.MirrorCS", {"start": v(68.14, 226.38) * mm, "end": v(109.25, 226.38) * mm, "construction": true});
            skLineSegment(sketch, "E92.MirrorCS", {"start": v(94.05, 208.38) * mm, "end": v(94.05, 238.38) * mm, "construction": true});
            skLineSegment(sketch, "E93.MirrorCS", {"start": v(79.05, 238.38) * mm, "end": v(79.05, 226.38) * mm});
            skLineSegment(sketch, "E94.MirrorCS", {"start": v(79.05, 226.38) * mm, "end": v(61.05, 208.38) * mm});
            skArc(sketch, "E95.MirrorCS", {"start": v(79.05, 238.38) * mm, "mid": v(94.05, 253.38) * mm, "end": v(109.05, 238.38) * mm});
            skSolve(sketch);
        }
        {
            var Q0;
            Q0=makeQuery(id+"F16.imprint","IMPRINT",FACE,{"disambiguationData":[TD([[makeQuery(id+"F16.imprint","IMPRINT",EDGE,{"derivedFrom":sQuery(id+"F16.wireOp",EDGE,"E80")}),-1.0]])]});
            var Q1;
            Q1=makeQuery(id+"F16.imprint","IMPRINT",FACE,{"disambiguationData":[TD([[makeQuery(id+"F16.imprint","IMPRINT",EDGE,{"derivedFrom":makeQuery(id+"F1.opExtrude","CAP_EDGE",EDGE,{"disambiguationData":[OSD([sQuery(id+"F0.wireOp",EDGE,"E1.left")])],"isStart":true})}),-1.0]])]});
            var Q2;
            Q2=makeQuery(id+"F16.imprint","IMPRINT",FACE,{"disambiguationData":[TD([[makeQuery(id+"F16.imprint","IMPRINT",EDGE,{"derivedFrom":sQuery(id+"F16.wireOp",EDGE,"E88.MirrorCS")}),-1.0]])]});
            var Q3;
            Q3=makeQuery(id+"F2.opExtrude","CAP_FACE",FACE,{"disambiguationData":[OSD([sQuery(id+"F0.wireOp",EDGE,"E12"),sQuery(id+"F0.wireOp",EDGE,"E13"),sQuery(id+"F0.wireOp",EDGE,"E14"),sQuery(id+"F0.wireOp",EDGE,"E15"),sQuery(id+"F0.wireOp",EDGE,"E17.filletArc"),sQuery(id+"F0.wireOp",EDGE,"E18.filletArc"),sQuery(id+"F0.wireOp",EDGE,"E19.filletArc"),sQuery(id+"F0.wireOp",EDGE,"E20.filletArc"),sQuery(id+"F0.wireOp",EDGE,"E25.0"),sQuery(id+"F0.wireOp",EDGE,"E25.1"),sQuery(id+"F0.wireOp",EDGE,"E25.2"),sQuery(id+"F0.wireOp",EDGE,"E25.3"),sQuery(id+"F0.wireOp",EDGE,"E25.4"),sQuery(id+"F0.wireOp",EDGE,"E25.5"),sQuery(id+"F0.wireOp",EDGE,"E25.6"),sQuery(id+"F0.wireOp",EDGE,"E25.7")])],"isStart":false});
            extrude(context, id + "F17", {"entities" : qUnion([Q0, Q1, Q2]), "endBound" : BoundingType.UP_TO_SURFACE, "endBoundEntityFace" : qUnion([Q3]), "depth" : 25 * mm});
        }
    });
